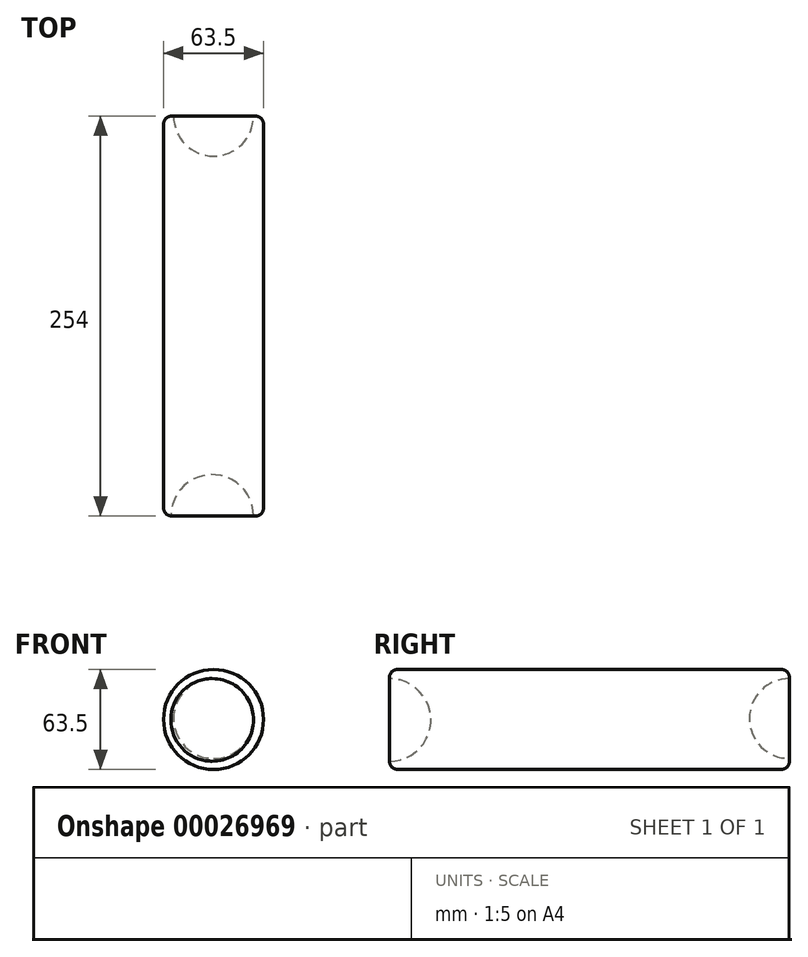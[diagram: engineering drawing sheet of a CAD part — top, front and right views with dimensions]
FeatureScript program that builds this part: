
annotation { "Feature Type Name" : "Feature", "Feature Type Description" : "" }
export const myFeature = defineFeature(function(context is Context, id is Id, definition is map)
    precondition{}
    {
        {
            var Q0;
            Q0=qCreatedBy(makeId("Front.planeOp"),FACE);
            var sketch = newSketch(context, id + "F0", { "sketchPlane" : qUnion([Q0])});
            skCircle(sketch, "E0", {"center": v(-15.5, 20.71) * mm, "radius": 31.75 * mm});
            skSolve(sketch);
        }
        {
            var Q0;
            Q0=makeQuery(id+"F0.imprint","IMPRINT",FACE,{"disambiguationData":[TD([[makeQuery(id+"F0.imprint","IMPRINT",EDGE,{"derivedFrom":sQuery(id+"F0.wireOp",EDGE,"E0")}),1.0]])]});
            extrude(context, id + "F1", {"entities" : qUnion([Q0]), "depth" : 254 * mm});
        }
        {
            var Q0;
            Q0=makeQuery(id+"F1.opExtrude","CAP_FACE",FACE,{"disambiguationData":[OSD([sQuery(id+"F0.wireOp",EDGE,"E0")])],"isStart":false});
            var sketch = newSketch(context, id + "F2", { "sketchPlane" : qUnion([Q0])});
            skLineSegment(sketch, "E1", {"start": v(-16.36, 46.64) * mm, "end": v(-16.36, -5.81) * mm});
            skArc(sketch, "E2", {"start": v(-16.36, -5.81) * mm, "mid": v(9.9, 20.41) * mm, "end": v(-16.36, 46.64) * mm});
            skSolve(sketch);
        }
        {
            var Q0;
            Q0=makeQuery(id+"F1.opExtrude","CAP_FACE",FACE,{"disambiguationData":[OSD([sQuery(id+"F0.wireOp",EDGE,"E0")])],"isStart":true});
            var sketch = newSketch(context, id + "F3", { "sketchPlane" : qUnion([Q0])});
            skLineSegment(sketch, "E3", {"start": v(15.49, 46.7) * mm, "end": v(15.49, -4.1) * mm});
            skArc(sketch, "E4", {"start": v(15.49, -4.1) * mm, "mid": v(40.89, 21.3) * mm, "end": v(15.49, 46.7) * mm});
            skSolve(sketch);
        }
        {
            var Q0;
            Q0=makeQuery(id+"F3.imprint","IMPRINT",FACE,{"disambiguationData":[TD([[makeQuery(id+"F3.imprint","IMPRINT",EDGE,{"derivedFrom":sQuery(id+"F3.wireOp",EDGE,"E3")}),1.0]])]});
            var Q1;
            Q1=sQuery(id+"F3.wireOp",EDGE,"E3");
            revolve(context, id + "F4", {"operationType" : NewBodyOperationType.REMOVE, "entities" : qUnion([Q0]), "axis" : qUnion([Q1]), "revolveType" : RevolveType.FULL, "oppositeDirection" : true});
        }
        {
            var Q0;
            Q0=makeQuery(id+"F2.imprint","IMPRINT",FACE,{"disambiguationData":[TD([[makeQuery(id+"F2.imprint","IMPRINT",EDGE,{"derivedFrom":sQuery(id+"F2.wireOp",EDGE,"E1")}),1.0]])]});
            var Q1;
            Q1=sQuery(id+"F2.wireOp",EDGE,"E1");
            revolve(context, id + "F5", {"operationType" : NewBodyOperationType.REMOVE, "entities" : qUnion([Q0]), "axis" : qUnion([Q1]), "revolveType" : RevolveType.FULL, "oppositeDirection" : true});
        }
        {
            var Q0;
            Q0=makeQuery(id+"F1.opExtrude","CAP_EDGE",EDGE,{"disambiguationData":[OSD([sQuery(id+"F0.wireOp",EDGE,"E0")])],"isStart":false});
            var Q1;
            Q1=makeQuery(id+"F1.opExtrude","CAP_EDGE",EDGE,{"disambiguationData":[OSD([sQuery(id+"F0.wireOp",EDGE,"E0")])],"isStart":true});
            fillet(context, id + "F6", {"entities" : qUnion([Q0, Q1]), "radius" : 5.08 * mm, "tangentPropagation" : true, "allowEdgeOverflow" : false});
        }
    });
